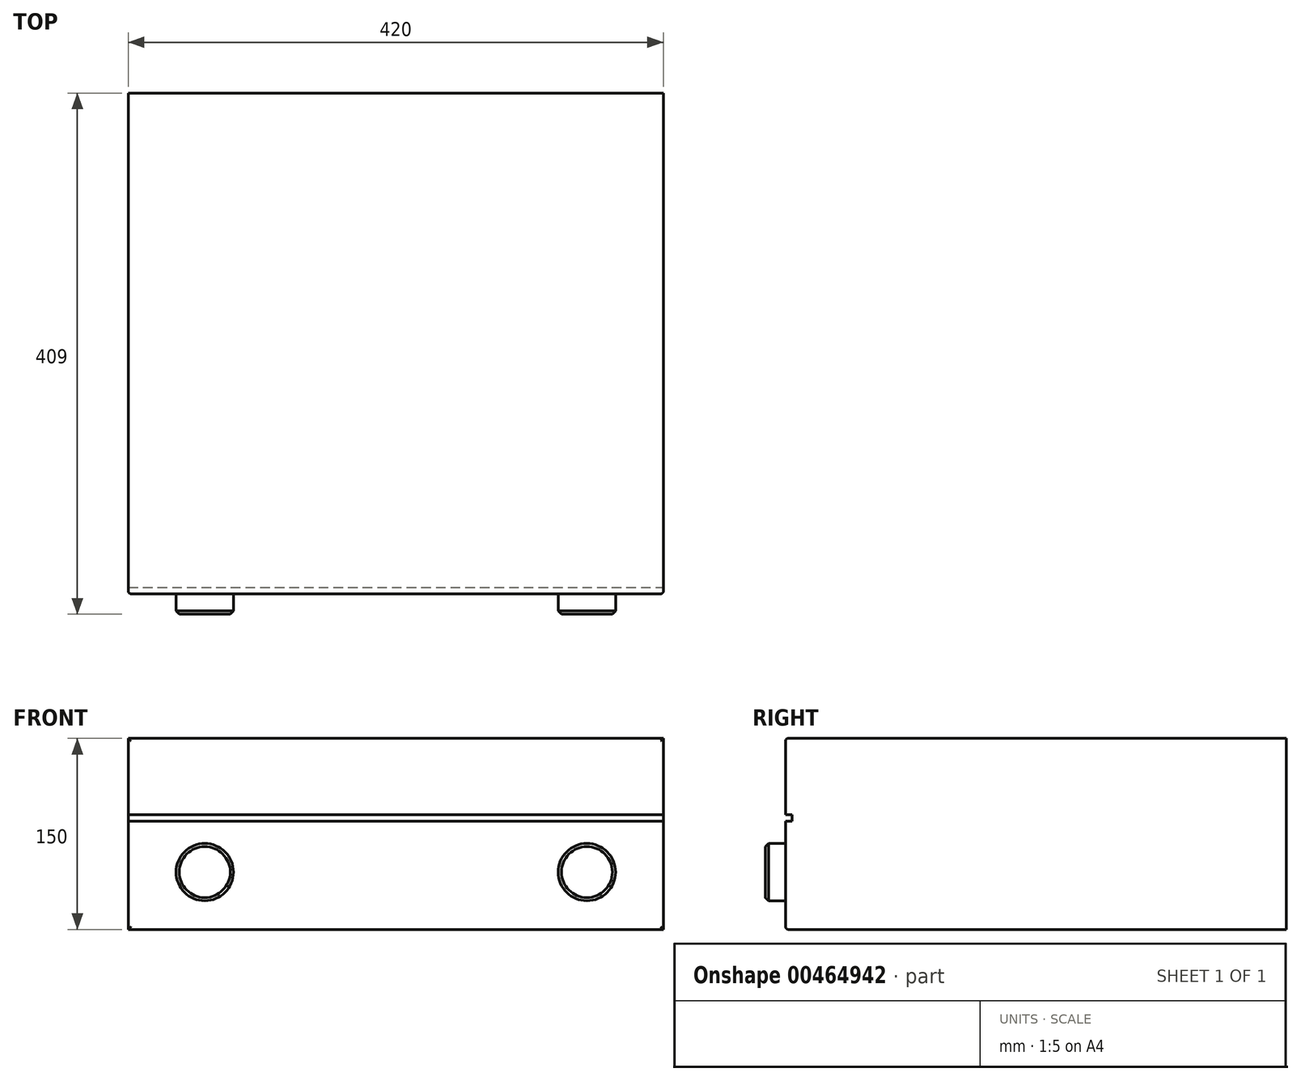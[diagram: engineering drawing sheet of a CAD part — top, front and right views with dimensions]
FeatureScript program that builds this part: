
annotation { "Feature Type Name" : "Feature", "Feature Type Description" : "" }
export const myFeature = defineFeature(function(context is Context, id is Id, definition is map)
    precondition{}
    {
        {
            var Q0;
            Q0=qCreatedBy(makeId("Front.planeOp"),FACE);
            var sketch = newSketch(context, id + "F0", { "sketchPlane" : qUnion([Q0])});
            skLineSegment(sketch, "E0.bottom", {"start": v(210, 75) * mm, "end": v(-210, 75) * mm});
            skLineSegment(sketch, "E0.top", {"start": v(210, -75) * mm, "end": v(-210, -75) * mm});
            skLineSegment(sketch, "E0.left", {"start": v(210, 75) * mm, "end": v(210, -75) * mm});
            skLineSegment(sketch, "E0.right", {"start": v(-210, 75) * mm, "end": v(-210, -75) * mm});
            skPoint(sketch, "E0.middle", {"position": v(0, 0) * mm});
            skSolve(sketch);
        }
        {
            var Q0;
            Q0 = qSketchRegion(id + "F0", true);
            extrude(context, id + "F1", {"entities" : qUnion([Q0]), "oppositeDirection" : true, "depth" : 393 * mm});
        }
        {
            var Q0;
            Q0=makeQuery(id+"F1.opExtrude","CAP_FACE",FACE,{"disambiguationData":[OSD([sQuery(id+"F0.wireOp",EDGE,"E0.bottom"),sQuery(id+"F0.wireOp",EDGE,"E0.top"),sQuery(id+"F0.wireOp",EDGE,"E0.left"),sQuery(id+"F0.wireOp",EDGE,"E0.right")])],"isStart":true});
            fillet(context, id + "F2", {"entities" : qUnion([Q0]), "radius" : 2 * mm, "tangentPropagation" : true, "allowEdgeOverflow" : false});
        }
        {
            var Q0;
            Q0=makeQuery(id+"F1.opExtrude","CAP_FACE",FACE,{"disambiguationData":[OSD([sQuery(id+"F0.wireOp",EDGE,"E0.bottom"),sQuery(id+"F0.wireOp",EDGE,"E0.top"),sQuery(id+"F0.wireOp",EDGE,"E0.left"),sQuery(id+"F0.wireOp",EDGE,"E0.right")])],"isStart":true});
            var sketch = newSketch(context, id + "F3", { "sketchPlane" : qUnion([Q0])});
            skCircle(sketch, "E1", {"center": v(-150, -30) * mm, "radius": 22.5 * mm});
            skCircle(sketch, "E2", {"center": v(150, -30) * mm, "radius": 22.5 * mm});
            skLineSegment(sketch, "E3", {"start": v(-150, -30) * mm, "end": v(150, -30) * mm, "construction": true});
            skSolve(sketch);
        }
        {
            var Q0;
            Q0 = qSketchRegion(id + "F3", true);
            extrude(context, id + "F4", {"entities" : qUnion([Q0]), "operationType" : NewBodyOperationType.ADD, "depth" : 16 * mm});
        }
        {
            var Q0;
            Q0=makeQuery(id+"F4.opExtrude","CAP_FACE",FACE,{"disambiguationData":[OSD([sQuery(id+"F3.wireOp",EDGE,"E1")])],"isStart":false});
            var Q1;
            Q1=makeQuery(id+"F4.opExtrude","CAP_FACE",FACE,{"disambiguationData":[OSD([sQuery(id+"F3.wireOp",EDGE,"E2")])],"isStart":false});
            chamfer(context, id + "F5", {"entities" : qUnion([Q0, Q1]), "width" : 2.5 * mm, "tangentPropagation" : true});
        }
        {
            var Q0;
            Q0=qCreatedBy(makeId("Right.planeOp"),FACE);
            var sketch = newSketch(context, id + "F6", { "sketchPlane" : qUnion([Q0])});
            skLineSegment(sketch, "E4.bottom", {"start": v(5, 15) * mm, "end": v(0, 15) * mm});
            skLineSegment(sketch, "E4.top", {"start": v(5, 10) * mm, "end": v(0, 10) * mm});
            skLineSegment(sketch, "E4.left", {"start": v(5, 10) * mm, "end": v(5, 15) * mm});
            skLineSegment(sketch, "E4.right", {"start": v(0, 10) * mm, "end": v(0, 15) * mm});
            skPoint(sketch, "E4.middle", {"position": v(2.5, 12.5) * mm});
            skSolve(sketch);
        }
        {
            var Q0;
            Q0 = qSketchRegion(id + "F6", true);
            extrude(context, id + "F7", {"entities" : qUnion([Q0]), "operationType" : NewBodyOperationType.REMOVE, "endBound" : BoundingType.SYMMETRIC, "oppositeDirection" : true, "depth" : 500 * mm});
        }
    });
